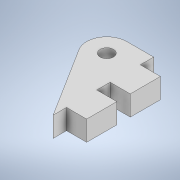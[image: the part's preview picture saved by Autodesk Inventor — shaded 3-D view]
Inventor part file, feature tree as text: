
AUTODESK INVENTOR PART (.ipt)
format: ipt  version: 2020 (Build 240168000, 168)  size: 120,320 bytes
history: native  units: in
note: dims shown in document units (in); Inventor stores cm internally (conversion verified against a paired STEP export)
features: extrude x3, sketch x3
ambient origin geometry x8: Origin, YZ Plane, XZ Plane, XY Plane, X Axis, Y Axis, Z Axis, Center Point
bodies: Solid1 (feature_tree)
feature tree (6):
  extrude  "Extrusion1"  Depth=0.1181in
  extrude  "Extrusion2"  Depth=0.1181in TaperAngle=0.0deg
  extrude  "Extrusion3"  Depth=0.1181in
  sketch  "Sketch1"  dims[d0=0.1772in d1=0.1181in]
  sketch  "Sketch2"  dims[d2=0.0394in d3=0.1181in d4=0.0in]
  sketch  "Sketch3"  dims[d5=0.0787in d6=0.5906in d10=0.1181in d11=0.1575in d12=0.1181in d13=0.0in d14=0.0787in d15=0.1181in d16=0.0in]
